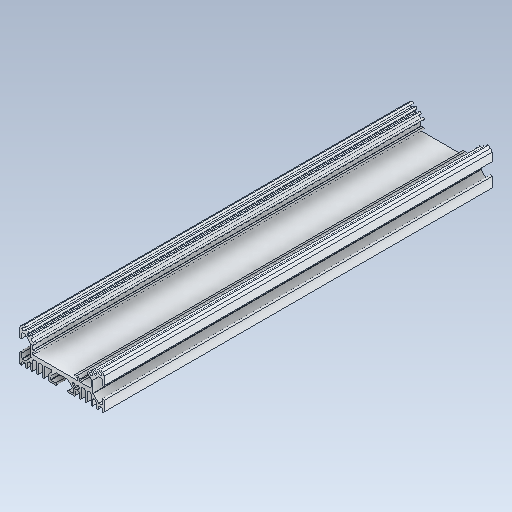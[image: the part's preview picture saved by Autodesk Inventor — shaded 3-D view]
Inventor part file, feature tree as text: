
AUTODESK INVENTOR PART (.ipt)
format: ipt  version: 2020 (Build 240168000, 168)  size: 292,352 bytes
history: native  units: mm
features: fillet x1
ambient origin geometry x8: Origin, YZ Plane, XZ Plane, XY Plane, X Axis, Y Axis, Z Axis, Center Point
bodies: Solid1 (feature_tree)
feature tree (1):
  fillet  "Fillet3"  [1 undecoded]
note: 1 required parameter value undecoded (feature->parameter linkage not recoverable at this tier; creation-order binding heuristic only, values carry confidence <= 0.55)
